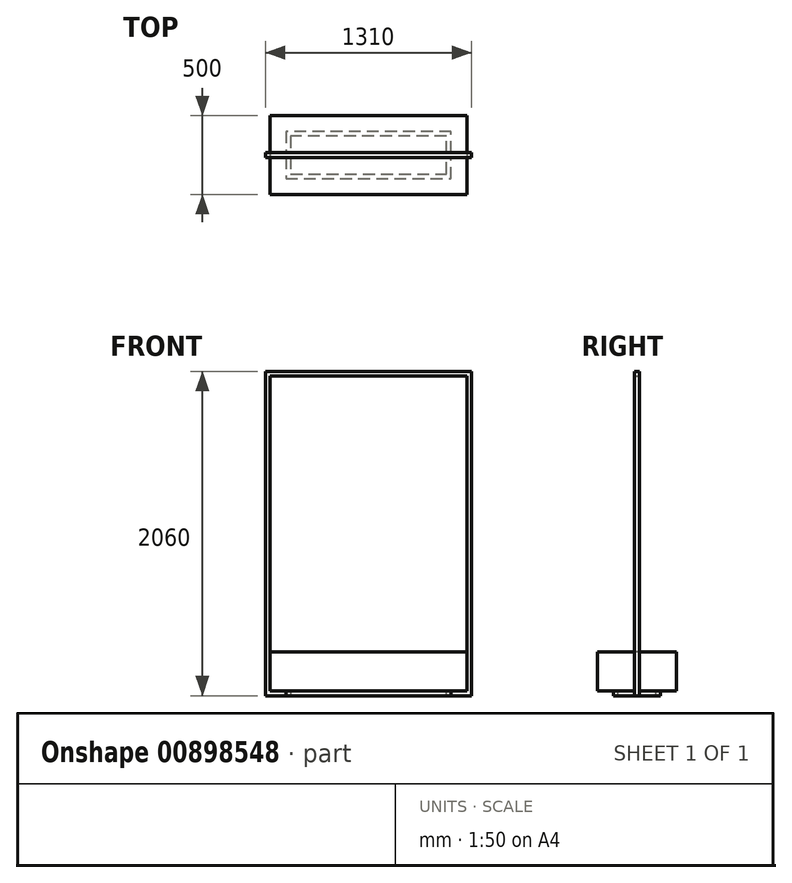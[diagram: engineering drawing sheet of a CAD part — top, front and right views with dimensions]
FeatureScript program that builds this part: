
annotation { "Feature Type Name" : "Feature", "Feature Type Description" : "" }
export const myFeature = defineFeature(function(context is Context, id is Id, definition is map)
    precondition{}
    {
        {
            var Q0;
            Q0=qCreatedBy(makeId("Top.planeOp"),FACE);
            var sketch = newSketch(context, id + "F0", { "sketchPlane" : qUnion([Q0])});
            skLineSegment(sketch, "E0.bottom", {"start": v(-625, 250) * mm, "end": v(625, 250) * mm});
            skLineSegment(sketch, "E0.top", {"start": v(-625, -250) * mm, "end": v(625, -250) * mm});
            skLineSegment(sketch, "E0.left", {"start": v(-625, 250) * mm, "end": v(-625, -250) * mm});
            skLineSegment(sketch, "E0.right", {"start": v(625, 250) * mm, "end": v(625, -250) * mm});
            skLineSegment(sketch, "E1", {"start": v(-625, 250) * mm, "end": v(625, -250) * mm, "construction": true});
            skSolve(sketch);
        }
        {
            var Q0;
            Q0=qSketchRegion(id+"F0",true);
            extrude(context, id + "F1", {"entities" : qUnion([Q0]), "depth" : 250 * mm, "offsetDistance" : 25 * mm});
        }
        {
            var Q0;
            Q0=qCreatedBy(makeId("Front.planeOp"),FACE);
            var sketch = newSketch(context, id + "F2", { "sketchPlane" : qUnion([Q0])});
            skLineSegment(sketch, "E2", {"start": v(625, 0) * mm, "end": v(625, 2000) * mm});
            skLineSegment(sketch, "E3", {"start": v(625, 2000) * mm, "end": v(-625, 2000) * mm});
            skLineSegment(sketch, "E4", {"start": v(-625, 2000) * mm, "end": v(-625, 0) * mm});
            skLineSegment(sketch, "E5", {"start": v(-625, 0) * mm, "end": v(625, 0) * mm});
            skLineSegment(sketch, "E6.0", {"start": v(655, 2030) * mm, "end": v(-655, 2030) * mm});
            skLineSegment(sketch, "E6.1", {"start": v(655, -30) * mm, "end": v(655, 2030) * mm});
            skLineSegment(sketch, "E6.2", {"start": v(-655, -30) * mm, "end": v(655, -30) * mm});
            skLineSegment(sketch, "E6.3", {"start": v(-655, 2030) * mm, "end": v(-655, -30) * mm});
            skSolve(sketch);
        }
        {
            var Q0;
            Q0=qSketchRegion(id+"F2",true);
            extrude(context, id + "F3", {"entities" : qUnion([Q0]), "endBound" : BoundingType.SYMMETRIC, "depth" : 30 * mm, "offsetDistance" : 25 * mm});
        }
        {
            var Q0;
            Q0=makeQuery(id+"F1.opExtrude","CAP_FACE",FACE,{"disambiguationData":[OSD([sQuery(id+"F0.wireOp",EDGE,"E0.bottom"),sQuery(id+"F0.wireOp",EDGE,"E0.top"),sQuery(id+"F0.wireOp",EDGE,"E0.left"),sQuery(id+"F0.wireOp",EDGE,"E0.right")])],"isStart":true});
            var sketch = newSketch(context, id + "F4", { "sketchPlane" : qUnion([Q0])});
            skLineSegment(sketch, "E7", {"start": v(525, 150) * mm, "end": v(525, -150) * mm});
            skLineSegment(sketch, "E8", {"start": v(525, -150) * mm, "end": v(-525, -150) * mm});
            skLineSegment(sketch, "E9", {"start": v(-525, -150) * mm, "end": v(-525, 150) * mm});
            skLineSegment(sketch, "E10", {"start": v(-525, 150) * mm, "end": v(525, 150) * mm});
            skLineSegment(sketch, "E11.0", {"start": v(-495, 120) * mm, "end": v(495, 120) * mm});
            skLineSegment(sketch, "E11.1", {"start": v(-495, -120) * mm, "end": v(-495, 120) * mm});
            skLineSegment(sketch, "E11.2", {"start": v(495, -120) * mm, "end": v(-495, -120) * mm});
            skLineSegment(sketch, "E11.3", {"start": v(495, 120) * mm, "end": v(495, -120) * mm});
            skSolve(sketch);
        }
        {
            var Q0;
            Q0=qSketchRegion(id+"F4",true);
            extrude(context, id + "F5", {"entities" : qUnion([Q0]), "operationType" : NewBodyOperationType.ADD, "depth" : 30 * mm, "offsetDistance" : 25 * mm});
        }
    });
